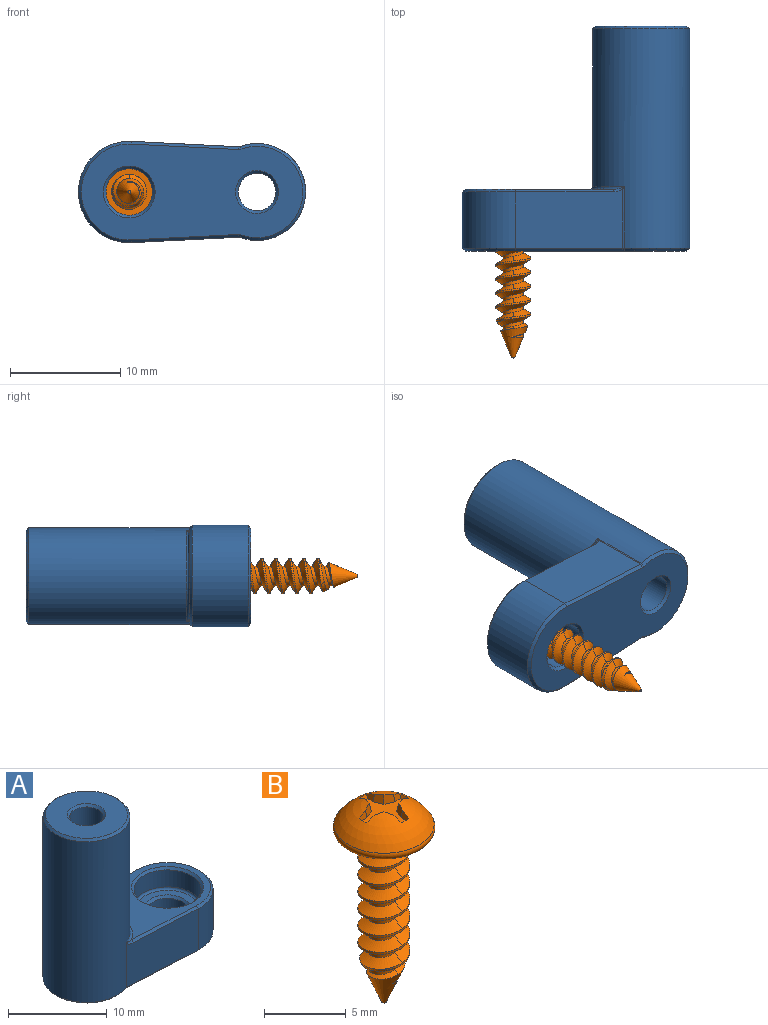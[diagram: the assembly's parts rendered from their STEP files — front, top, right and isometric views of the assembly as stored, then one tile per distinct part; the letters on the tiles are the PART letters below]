
ASSEMBLY  parts=2 mates=1
PART A: 38 faces, bbox 20.7x9.8x20.5 mm
  f0: cylinder r=4.4mm len=19.9mm, axis (0,0,-1), area 490.5mm2, adj f16,f17,f18,f29,f37
  f1: plane 8.3x8.3mm, normal (0,0,1), area 42.2mm2, adj f36,f37
  f2: plane 20.1x8.7mm, normal (0,0,-1), area 122.5mm2, adj f26,f27,f28,f29,f30,f31,f32,f33
  f3: plane 9.79x5.46mm, normal (-0.05,-1,0), area 49.7mm2, adj f4,f18,f23,f24,f26
  f4: cylinder r=4.6mm len=9.2mm, axis (0,0,-1), area 76.1mm2, adj f3,f5,f22,f28
  f5: plane 9.78x5.45mm, normal (-0.05,1,0), area 49.7mm2, adj f4,f16,f20,f21,f30
  f6: plane 13.41x8.7mm, normal (0,0,1), area 51.1mm2, adj f17,f21,f22,f23,f35
  f7: cylinder r=2.1mm len=4.2mm, axis (0,0,1), area 33mm2, adj f32,f34
  f8: plane 6.3x6.3mm, normal (0,0,1), area 13.8mm2, adj f15,f34
  f9: cylinder r=3.4mm len=6.8mm, axis (0,0,1), area 44.9mm2, adj f15,f35
  f10: cylinder r=1.7mm len=3.4mm, axis (0,0,1), area 29.4mm2, adj f14,f36
  f11: cylinder r=1.7mm len=14.15mm, axis (0,0,1), area 151.1mm2, adj f12,f33
  f12: plane 7x7mm, normal (0,0,1), area 29.4mm2, adj f11,f13
  f13: cylinder r=3.5mm len=7mm, axis (0,0,1), area 66mm2, adj f12,f14
  f14: plane 7x7mm, normal (0,0,-1), area 29.4mm2, adj f10,f13
  f15: torus R=3.15mm, axis (0,0,1), area 8.2mm2, adj f8,f9
  f16: cylinder r=0.25mm len=5.6mm, axis (0,0,-1), area 0.6mm2, adj f0,f5,f19,f31
  f17: torus R=4.65mm, axis (0,0,1), area 3.9mm2, adj f0,f6,f19,f20,f24,f25
  f18: cylinder r=0.25mm len=5.6mm, axis (0,0,-1), area 0.6mm2, adj f0,f3,f25,f27
  f19: bspline ~0.21x0.2mm, area 0mm2, adj f16,f17,f20
  f20: bspline ~0.89x0.4mm, area 0.2mm2, adj f5,f17,f19,f21
  f21: plane 8.86x0.7mm, normal (-0.04,0.71,0.71), area 3.1mm2, adj f5,f6,f20,f22
  f22: cone r=4.35mm half-angle=45deg, axis (0,0,-1), area 5.1mm2, adj f4,f6,f21,f23
  f23: plane 8.86x0.7mm, normal (-0.04,-0.71,0.71), area 3.1mm2, adj f3,f6,f22,f24
  f24: bspline ~0.89x0.4mm, area 0.2mm2, adj f3,f17,f23,f25
  f25: bspline ~0.21x0.2mm, area 0mm2, adj f17,f18,f24
  f26: plane 9.73x0.74mm, normal (-0.04,-0.71,-0.71), area 3.4mm2, adj f2,f3,f27,f28
  f27: cone r=0.5mm half-angle=45deg, axis (0,0,-1), area 0.1mm2, adj f2,f18,f26,f29
  f28: cone r=4.6mm half-angle=45deg, axis (0,0,1), area 5.1mm2, adj f2,f4,f26,f30
  f29: cone r=4.4mm half-angle=45deg, axis (0,0,1), area 5.8mm2, adj f0,f2,f27,f31
  f30: plane 9.73x0.74mm, normal (-0.04,0.71,-0.71), area 3.4mm2, adj f2,f5,f28,f31
  f31: cone r=0.5mm half-angle=45deg, axis (0,0,-1), area 0.1mm2, adj f2,f16,f29,f30
  f32: cone r=2.1mm half-angle=45deg, axis (0,0,-1), area 4.9mm2, adj f2,f7
  f33: cone r=1.95mm half-angle=45deg, axis (0,0,-1), area 4.1mm2, adj f2,f11
  f34: cone r=2.1mm half-angle=45deg, axis (0,0,1), area 4.9mm2, adj f7,f8
  f35: cone r=3.4mm half-angle=45deg, axis (0,0,1), area 7.8mm2, adj f6,f9
  f36: cone r=1.7mm half-angle=45deg, axis (0,0,1), area 4.1mm2, adj f1,f10
  f37: cone r=4.15mm half-angle=45deg, axis (0,0,-1), area 9.5mm2, adj f0,f1
PART B: 47 faces, bbox 7.1x7.1x15.2 mm
  f0: cylinder r=0.9mm len=10.83mm, axis (0,0,-1), area 15.3mm2, adj f2,f3,f4,f5,f6,f9,f10,f11
  f1: cylinder r=1.59mm len=9.17mm, axis (0,0,-1), area 11.4mm2, adj f2,f3,f6,f9,f10,f11,f12,f13
  f2: bspline ~3.67x3.18mm, area 3.1mm2, adj f0,f1,f4,f21,f23,f24
  f3: bspline ~3.67x3.18mm, area 4.7mm2, adj f0,f1,f5,f22,f23,f24
  f4: cylinder r=1.9mm len=0.18mm, axis (-0.28,0.81,-0.52), area 0mm2, adj f0,f2,f24
  f5: bspline ~2.93x2.53mm, area 1mm2, adj f0,f3,f24
  f6: plane 5.82x5.82mm, normal (0,0,-1), area 18.9mm2, adj f0,f1,f7,f11,f12
  f7: torus R=2.74mm, axis (0,0,-1), area 14.9mm2, adj f6,f8
  f8: sphere r=3.6mm, area 32.1mm2, adj f7,f26,f27,f28,f29,f30,f31,f33
  f9: bspline ~3.67x3.18mm, area 9.4mm2, adj f0,f1,f11,f13
  f10: bspline ~3.67x3.18mm, area 9.4mm2, adj f0,f1,f12,f14
  f11: bspline ~3.67x3.18mm, area 5.2mm2, adj f0,f1,f6,f9
  f12: bspline ~3.17x2.2mm, area 2.6mm2, adj f0,f1,f6,f10
  f13: bspline ~3.67x3.18mm, area 6.3mm2, adj f0,f1,f9,f15
  f14: bspline ~3.67x3.18mm, area 6.3mm2, adj f0,f1,f10,f16
  f15: bspline ~3.67x3.18mm, area 6.3mm2, adj f0,f1,f13,f17
  f16: bspline ~3.67x3.18mm, area 6.3mm2, adj f0,f1,f14,f18
  f17: bspline ~3.67x3.18mm, area 6.3mm2, adj f0,f1,f15,f19
  f18: bspline ~3.67x3.18mm, area 6.3mm2, adj f0,f1,f16,f20
  f19: bspline ~3.67x3.18mm, area 6.3mm2, adj f0,f1,f17,f21
  f20: bspline ~3.67x3.18mm, area 6.3mm2, adj f0,f1,f18,f22
  f21: bspline ~3.67x3.18mm, area 6.3mm2, adj f0,f1,f2,f19
  f22: bspline ~3.67x3.18mm, area 6.3mm2, adj f0,f1,f3,f20
  f23: cone r=1.59mm half-angle=22.5deg, axis (0,0,1), area 2.3mm2, adj f1,f2,f3,f24
  f24: cone r=1.59mm half-angle=22.5deg, axis (0,0,1), area 10mm2, adj f0,f2,f3,f4,f5,f23,f25
  f25: plane 0.25x0.25mm, normal (0,0,-1), area 0.1mm2, adj f24
  f26: cone r=2.07mm half-angle=25deg, axis (0,0,1), area 0.2mm2, adj f8,f27,f32,f37
  f27: plane 0.65x0.55mm, normal (-0.98,0,0.17), area 0.2mm2, adj f8,f26,f28,f32
  f28: plane 0.78x0.75mm, normal (-0.91,-0.38,0.17), area 0.4mm2, adj f8,f27,f29,f32
  f29: plane 0.78x0.75mm, normal (-0.38,-0.91,0.17), area 0.4mm2, adj f8,f28,f30,f32
  f30: plane 0.65x0.55mm, normal (0,-0.98,0.17), area 0.2mm2, adj f8,f29,f31,f32
  f31: cone r=2.07mm half-angle=25deg, axis (0,0,1), area 0.2mm2, adj f8,f30,f32,f43
  f32: plane 3.45x3.45mm, normal (0,0,1), area 4.5mm2, adj f26,f27,f28,f29,f30,f31,f33,f34
  f33: cone r=2.07mm half-angle=25deg, axis (0,0,1), area 0.2mm2, adj f8,f32,f34,f42
  f34: plane 0.65x0.55mm, normal (0,-0.98,0.17), area 0.2mm2, adj f8,f32,f33,f35
  f35: plane 0.78x0.75mm, normal (0.38,-0.91,0.17), area 0.4mm2, adj f8,f32,f34,f36
  f36: plane 0.78x0.75mm, normal (0.91,-0.38,0.17), area 0.4mm2, adj f8,f32,f35,f37
  f37: plane 0.65x0.55mm, normal (0.98,0,0.17), area 0.2mm2, adj f8,f26,f32,f36
  f38: cone r=2.07mm half-angle=25deg, axis (0,0,1), area 0.2mm2, adj f8,f32,f39,f46
  f39: plane 0.65x0.55mm, normal (0.98,0,0.17), area 0.2mm2, adj f8,f32,f38,f40
  f40: plane 0.78x0.75mm, normal (0.91,0.38,0.17), area 0.4mm2, adj f8,f32,f39,f41
  f41: plane 0.78x0.75mm, normal (0.38,0.91,0.17), area 0.4mm2, adj f8,f32,f40,f42
  f42: plane 0.65x0.55mm, normal (0,0.98,0.17), area 0.2mm2, adj f8,f32,f33,f41
  f43: plane 0.65x0.55mm, normal (0,0.98,0.17), area 0.2mm2, adj f8,f31,f32,f44
  f44: plane 0.78x0.75mm, normal (-0.38,0.91,0.17), area 0.4mm2, adj f8,f32,f43,f45
  f45: plane 0.78x0.75mm, normal (-0.91,0.38,0.17), area 0.4mm2, adj f8,f32,f44,f46
  f46: plane 0.65x0.55mm, normal (-0.98,0,0.17), area 0.2mm2, adj f8,f32,f38,f45
PLACE A rot(axis=(0,0.71,0.71),180deg) t=(0,-20.4,0)mm
PLACE B rot(axis=(-1,0,0),90deg) t=(-11.6,-17.4,0)mm
MATE fastened B.f0 <-> A.f7  axis (0,-1,0) through (-11.6,-17.4,0)mm
